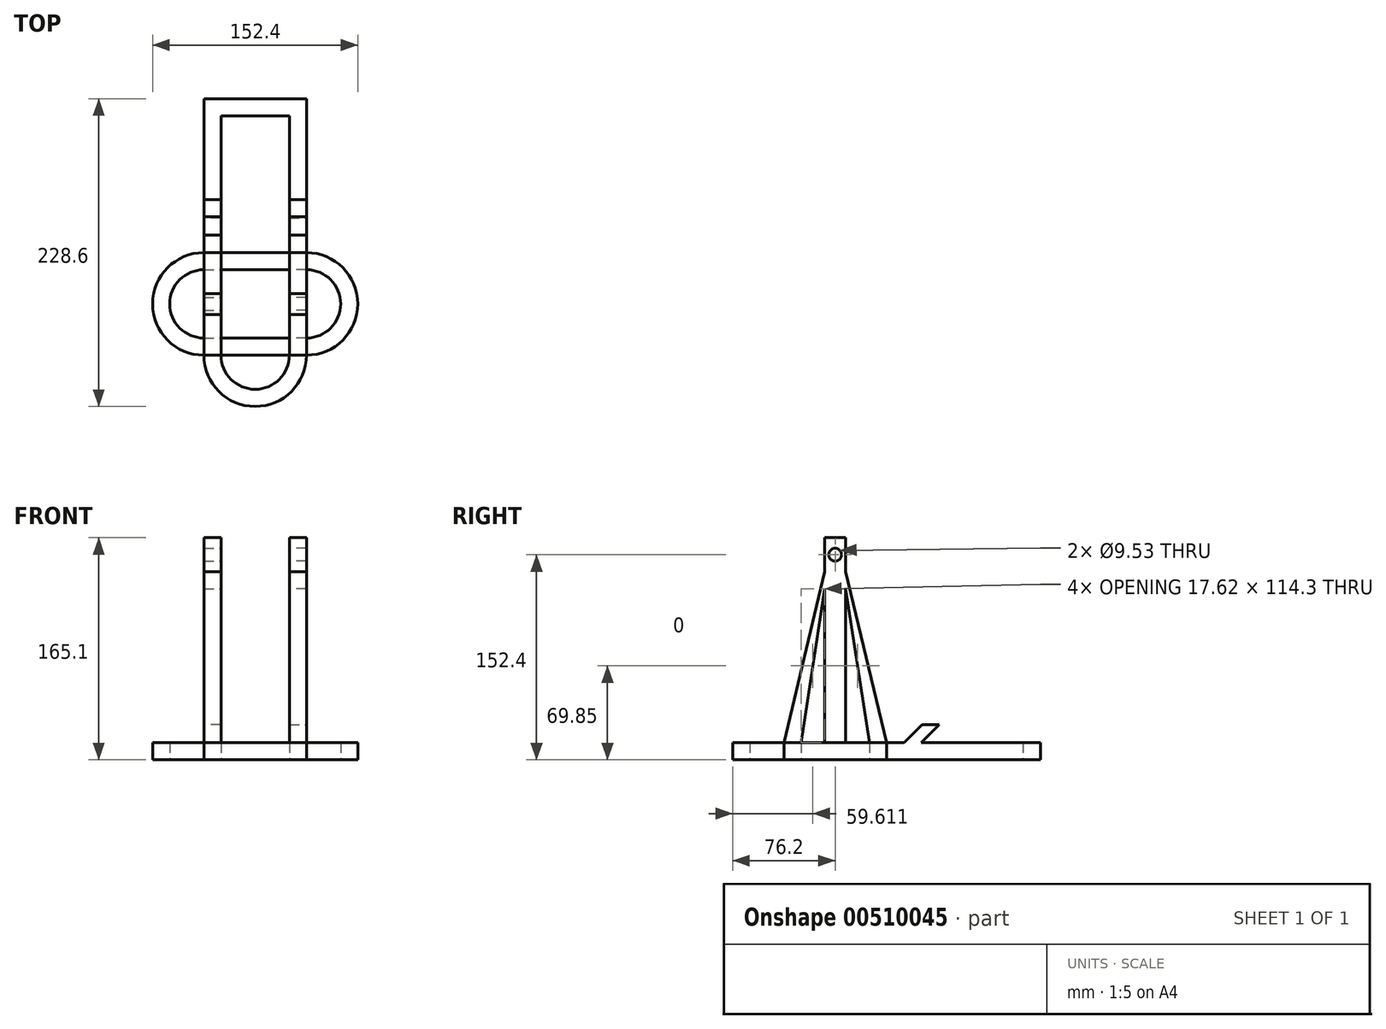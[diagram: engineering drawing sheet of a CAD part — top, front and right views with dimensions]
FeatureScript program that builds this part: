
annotation { "Feature Type Name" : "Feature", "Feature Type Description" : "" }
export const myFeature = defineFeature(function(context is Context, id is Id, definition is map)
    precondition{}
    {
        {
            var Q0;
            Q0=qCreatedBy(makeId("Top.planeOp"),FACE);
            var sketch = newSketch(context, id + "F0", { "sketchPlane" : qUnion([Q0])});
            skLineSegment(sketch, "E0.bottom", {"start": v(25.4, 38.1) * mm, "end": v(-25.4, 38.1) * mm});
            skLineSegment(sketch, "E0.top", {"start": v(38.1, -38.1) * mm, "end": v(-38.1, -38.1) * mm});
            skPoint(sketch, "E0.middle", {"position": v(0, 0) * mm});
            skArc(sketch, "E1", {"start": v(-38.1, 38.1) * mm, "mid": v(-76.2, 0) * mm, "end": v(-38.1, -38.1) * mm});
            skArc(sketch, "E2", {"start": v(38.1, -38.1) * mm, "mid": v(76.2, 0) * mm, "end": v(38.1, 38.1) * mm});
            skLineSegment(sketch, "E3.bottom", {"start": v(25.4, 25.4) * mm, "end": v(-25.4, 25.4) * mm});
            skLineSegment(sketch, "E3.top", {"start": v(25.4, -25.4) * mm, "end": v(-25.4, -25.4) * mm});
            skLineSegment(sketch, "E3.left", {"start": v(25.4, 25.4) * mm, "end": v(25.4, -25.4) * mm});
            skLineSegment(sketch, "E3.right", {"start": v(-25.4, 25.4) * mm, "end": v(-25.4, -25.4) * mm});
            skLineSegment(sketch, "E4", {"start": v(-38.1, 0) * mm, "end": v(-25.4, 0) * mm, "construction": true});
            skArc(sketch, "E5", {"start": v(-38.1, 25.4) * mm, "mid": v(-63.5, 0) * mm, "end": v(-38.1, -25.4) * mm});
            skArc(sketch, "E6", {"start": v(38.1, -25.4) * mm, "mid": v(63.5, 0) * mm, "end": v(38.1, 25.4) * mm});
            skLineSegment(sketch, "E7", {"start": v(-38.1, 25.4) * mm, "end": v(-38.1, -25.4) * mm});
            skLineSegment(sketch, "E8", {"start": v(38.1, 25.4) * mm, "end": v(38.1, -25.4) * mm});
            skLineSegment(sketch, "E9", {"start": v(25.4, 0) * mm, "end": v(38.1, 0) * mm});
            skLineSegment(sketch, "E10", {"start": v(0, 25.4) * mm, "end": v(0, 38.1) * mm, "construction": true});
            skLineSegment(sketch, "E11", {"start": v(-38.1, 38.1) * mm, "end": v(-38.1, 152.4) * mm});
            skLineSegment(sketch, "E12", {"start": v(25.4, 38.1) * mm, "end": v(25.4, 139.7) * mm});
            skLineSegment(sketch, "E13", {"start": v(38.1, 152.4) * mm, "end": v(38.1, 38.1) * mm});
            skLineSegment(sketch, "E14", {"start": v(-25.4, 139.7) * mm, "end": v(25.4, 139.7) * mm});
            skLineSegment(sketch, "E15.trimOffspring", {"start": v(-25.4, 139.7) * mm, "end": v(-25.4, 38.1) * mm});
            skLineSegment(sketch, "E16", {"start": v(0, 152.4) * mm, "end": v(0, 139.7) * mm});
            skLineSegment(sketch, "E17", {"start": v(-38.1, 152.4) * mm, "end": v(38.1, 152.4) * mm});
            skArc(sketch, "E18", {"start": v(-38.1, -38.1) * mm, "mid": v(0, -76.2) * mm, "end": v(38.1, -38.1) * mm});
            skArc(sketch, "E19", {"start": v(-25.4, -38.1) * mm, "mid": v(0, -63.5) * mm, "end": v(25.4, -38.1) * mm});
            skSolve(sketch);
        }
        {
            var Q0;
            Q0=makeQuery(id+"F0.imprint","IMPRINT",FACE,{"disambiguationData":[TD([[makeQuery(id+"F0.imprint","IMPRINT",EDGE,{"derivedFrom":sQuery(id+"F0.wireOp",EDGE,"E0.bottom")}),1.0]])]});
            var Q1;
            {var subQ0=sQuery(id+"F0.wireOp",EDGE,"E18");Q1=makeQuery(id+"F0.imprint","IMPRINT",FACE,{"disambiguationData":[TD([[makeQuery(id+"F0.imprint","IMPRINT",EDGE,{"derivedFrom":subQ0}),1.0]])]});}
            extrude(context, id + "F1", {"entities" : qUnion([Q0, Q1]), "depth" : 12.7 * mm});
        }
        {
            var Q0;
            Q0=makeQuery(id+"F1.opExtrude","CAP_FACE",FACE,{"disambiguationData":[OSD([sQuery(id+"F0.wireOp",EDGE,"E0.bottom"),sQuery(id+"F0.wireOp",EDGE,"E0.top"),sQuery(id+"F0.wireOp",EDGE,"E1"),sQuery(id+"F0.wireOp",EDGE,"E2"),sQuery(id+"F0.wireOp",EDGE,"E3.bottom"),sQuery(id+"F0.wireOp",EDGE,"E3.top"),sQuery(id+"F0.wireOp",EDGE,"E3.left"),sQuery(id+"F0.wireOp",EDGE,"E3.right"),sQuery(id+"F0.wireOp",EDGE,"E5"),sQuery(id+"F0.wireOp",EDGE,"E6"),sQuery(id+"F0.wireOp",EDGE,"E7"),sQuery(id+"F0.wireOp",EDGE,"E8"),sQuery(id+"F0.wireOp",EDGE,"E11"),sQuery(id+"F0.wireOp",EDGE,"eW0WrqK1-UAqt-hDgT-Up3a-L5sfFXZvn6og"),sQuery(id+"F0.wireOp",EDGE,"nnrCkwNE-DQRG-QEbR-UNsG-ga2bjcPdERez"),sQuery(id+"F0.wireOp",EDGE,"E12"),sQuery(id+"F0.wireOp",EDGE,"791204e0-3bb4-4a5e-b6f0-b63506c0d2d2"),sQuery(id+"F0.wireOp",EDGE,"E13"),sQuery(id+"F0.wireOp",EDGE,"E14"),sQuery(id+"F0.wireOp",EDGE,"Wew7rHin-LhuC-XoIG-YuWZ-GYeJMTqJVveu"),sQuery(id+"F0.wireOp",EDGE,"E15.trimOffspring"),sQuery(id+"F0.wireOp",EDGE,"b8e2c5c2-e6a5-42de-99a1-57f889a17564.trimOffspring")])],"isStart":false});
            var sketch = newSketch(context, id + "F2", { "sketchPlane" : qUnion([Q0])});
            skLineSegment(sketch, "E20.bottom", {"start": v(-25.4, 7.78) * mm, "end": v(-38.1, 7.78) * mm});
            skLineSegment(sketch, "E20.top", {"start": v(-25.4, -7.78) * mm, "end": v(-38.1, -7.78) * mm});
            skLineSegment(sketch, "E20.left", {"start": v(-25.4, 7.78) * mm, "end": v(-25.4, -7.78) * mm});
            skLineSegment(sketch, "E20.right", {"start": v(-38.1, 7.78) * mm, "end": v(-38.1, -7.78) * mm});
            skPoint(sketch, "E20.middle", {"position": v(-31.75, 0) * mm});
            skSolve(sketch);
        }
        {
            var Q0;
            Q0=qSketchRegion(id+"F2",true);
            extrude(context, id + "F3", {"entities" : qUnion([Q0]), "operationType" : NewBodyOperationType.ADD, "depth" : 152.4 * mm});
        }
        {
            var Q0;
            Q0=makeQuery(id+"F3.opExtrude","SWEPT_FACE",FACE,{"disambiguationData":[OSD([sQuery(id+"F2.wireOp",EDGE,"E20.top")])]});
            var sketch = newSketch(context, id + "F4", { "sketchPlane" : qUnion([Q0])});
            skLineSegment(sketch, "E21.bottom", {"start": v(-38.1, 139.7) * mm, "end": v(-25.4, 139.7) * mm});
            skLineSegment(sketch, "E21.top", {"start": v(-38.1, 127) * mm, "end": v(-25.4, 127) * mm});
            skLineSegment(sketch, "E21.left", {"start": v(-38.1, 139.7) * mm, "end": v(-38.1, 127) * mm});
            skLineSegment(sketch, "E21.right", {"start": v(-25.4, 139.7) * mm, "end": v(-25.4, 127) * mm});
            skSolve(sketch);
        }
        {
            var Q0;
            Q0=makeQuery(id+"F3.opExtrude","SWEPT_FACE",FACE,{"disambiguationData":[OSD([sQuery(id+"F2.wireOp",EDGE,"E20.bottom")])]});
            var sketch = newSketch(context, id + "F5", { "sketchPlane" : qUnion([Q0])});
            skLineSegment(sketch, "E22.0", {"start": v(25.4, 139.7) * mm, "end": v(25.4, 127) * mm});
            skLineSegment(sketch, "E23.0", {"start": v(38.1, 139.7) * mm, "end": v(25.4, 139.7) * mm});
            skLineSegment(sketch, "E24.0", {"start": v(38.1, 127) * mm, "end": v(25.4, 127) * mm});
            skLineSegment(sketch, "E25.0", {"start": v(38.1, 139.7) * mm, "end": v(38.1, 127) * mm});
            skSolve(sketch);
        }
        {
            var Q0;
            Q0=makeQuery(id+"F1.opExtrude","CAP_FACE",FACE,{"disambiguationData":[OSD([sQuery(id+"F0.wireOp",EDGE,"E0.bottom"),sQuery(id+"F0.wireOp",EDGE,"E0.top"),sQuery(id+"F0.wireOp",EDGE,"E1"),sQuery(id+"F0.wireOp",EDGE,"E2"),sQuery(id+"F0.wireOp",EDGE,"E3.bottom"),sQuery(id+"F0.wireOp",EDGE,"E3.top"),sQuery(id+"F0.wireOp",EDGE,"E3.left"),sQuery(id+"F0.wireOp",EDGE,"E3.right"),sQuery(id+"F0.wireOp",EDGE,"E5"),sQuery(id+"F0.wireOp",EDGE,"E6"),sQuery(id+"F0.wireOp",EDGE,"E7"),sQuery(id+"F0.wireOp",EDGE,"E8"),sQuery(id+"F0.wireOp",EDGE,"E11"),sQuery(id+"F0.wireOp",EDGE,"eW0WrqK1-UAqt-hDgT-Up3a-L5sfFXZvn6og"),sQuery(id+"F0.wireOp",EDGE,"nnrCkwNE-DQRG-QEbR-UNsG-ga2bjcPdERez"),sQuery(id+"F0.wireOp",EDGE,"E12"),sQuery(id+"F0.wireOp",EDGE,"791204e0-3bb4-4a5e-b6f0-b63506c0d2d2"),sQuery(id+"F0.wireOp",EDGE,"E13"),sQuery(id+"F0.wireOp",EDGE,"E14"),sQuery(id+"F0.wireOp",EDGE,"Wew7rHin-LhuC-XoIG-YuWZ-GYeJMTqJVveu"),sQuery(id+"F0.wireOp",EDGE,"E15.trimOffspring"),sQuery(id+"F0.wireOp",EDGE,"b8e2c5c2-e6a5-42de-99a1-57f889a17564.trimOffspring")])],"isStart":false});
            var sketch = newSketch(context, id + "F6", { "sketchPlane" : qUnion([Q0])});
            skPoint(sketch, "E26.oppositeSnap0", {"position": v(-25.4, -16.59) * mm});
            skLineSegment(sketch, "E26.bottom", {"start": v(-38.1, -25.4) * mm, "end": v(-25.4, -25.4) * mm});
            skLineSegment(sketch, "E26.top", {"start": v(-38.1, -38.1) * mm, "end": v(-25.4, -38.1) * mm});
            skLineSegment(sketch, "E26.left", {"start": v(-38.1, -25.4) * mm, "end": v(-38.1, -38.1) * mm});
            skLineSegment(sketch, "E26.right", {"start": v(-25.4, -25.4) * mm, "end": v(-25.4, -38.1) * mm});
            skLineSegment(sketch, "E27.bottom", {"start": v(-38.1, 38.1) * mm, "end": v(-25.4, 38.1) * mm});
            skLineSegment(sketch, "E27.top", {"start": v(-38.1, 25.4) * mm, "end": v(-25.4, 25.4) * mm});
            skLineSegment(sketch, "E27.left", {"start": v(-38.1, 38.1) * mm, "end": v(-38.1, 25.4) * mm});
            skLineSegment(sketch, "E27.right", {"start": v(-25.4, 38.1) * mm, "end": v(-25.4, 25.4) * mm});
            skArc(sketch, "E28.0", {"start": v(-38.1, 25.4) * mm, "mid": v(-63.5, 0) * mm, "end": v(-38.1, -25.4) * mm});
            skArc(sketch, "E29.0", {"start": v(-38.1, 38.1) * mm, "mid": v(-76.2, 0) * mm, "end": v(-38.1, -38.1) * mm});
            skSolve(sketch);
        }
        {
            var Q1;
            Q1=makeQuery(id+"F5.imprint","IMPRINT",FACE,{"disambiguationData":[TD([[makeQuery(id+"F5.imprint","IMPRINT",EDGE,{"derivedFrom":sQuery(id+"F5.wireOp",EDGE,"E22.0")}),1.0]])]});
            var Q2;
            Q2=makeQuery(id+"F6.imprint","IMPRINT",FACE,{"disambiguationData":[TD([[makeQuery(id+"F6.imprint","IMPRINT",EDGE,{"derivedFrom":sQuery(id+"F6.wireOp",EDGE,"E27.bottom")}),-1.0]])]});
            loft(context, id + "F7", {"operationType" : NewBodyOperationType.ADD, "sheetProfilesArray" : [{ "sheetProfileEntities" : qUnion([Q1]) }, { "sheetProfileEntities" : qUnion([Q2]) }]});
        }
        {
            var Q1;
            Q1=makeQuery(id+"F6.imprint","IMPRINT",FACE,{"disambiguationData":[TD([[makeQuery(id+"F6.imprint","IMPRINT",EDGE,{"derivedFrom":sQuery(id+"F6.wireOp",EDGE,"E26.bottom")}),-1.0]])]});
            var Q2;
            Q2=makeQuery(id+"F4.imprint","IMPRINT",FACE,{"disambiguationData":[TD([[makeQuery(id+"F4.imprint","IMPRINT",EDGE,{"derivedFrom":sQuery(id+"F4.wireOp",EDGE,"E21.bottom")}),-1.0]])]});
            loft(context, id + "F8", {"operationType" : NewBodyOperationType.ADD, "sheetProfilesArray" : [{ "sheetProfileEntities" : qUnion([Q1]) }, { "sheetProfileEntities" : qUnion([Q2]) }]});
        }
        {
            var Q0;
            Q0=makeQuery(id+"F1.opExtrude","SWEPT_FACE",FACE,{"disambiguationData":[OSD([sQuery(id+"F0.wireOp",EDGE,"E11")])]});
            var sketch = newSketch(context, id + "F9", { "sketchPlane" : qUnion([Q0])});
            skLineSegment(sketch, "E30", {"start": v(-63.94, 12.7) * mm, "end": v(-77.41, 26.17) * mm});
            skLineSegment(sketch, "E31", {"start": v(-77.41, 26.17) * mm, "end": v(-64.71, 26.17) * mm});
            skLineSegment(sketch, "E32", {"start": v(-64.71, 26.17) * mm, "end": v(-51.24, 12.7) * mm});
            skSolve(sketch);
        }
        {
            var Q0;
            {var subQ0=sQuery(id+"F9.wireOp",EDGE,"E30");Q0=makeQuery(id+"F9.imprint","IMPRINT",FACE,{"disambiguationData":[TD([[makeQuery(id+"F9.imprint","IMPRINT",EDGE,{"derivedFrom":subQ0}),-1.0]])]});}
            var Q1;
            Q1=makeQuery(id+"F1.opExtrude","SWEPT_FACE",FACE,{"disambiguationData":[OSD([sQuery(id+"F0.wireOp",EDGE,"E15.trimOffspring")])]});
            extrude(context, id + "F10", {"entities" : qUnion([Q0]), "operationType" : NewBodyOperationType.ADD, "endBound" : BoundingType.UP_TO_SURFACE, "oppositeDirection" : true, "endBoundEntityFace" : qUnion([Q1]), "depth" : 25.4 * mm});
        }
        {
            var Q0;
            {var subQ0=sQuery(id+"F2.wireOp",EDGE,"E20.left");var subQ1=sQuery(id+"F0.wireOp",EDGE,"E3.right");Q0=makeQuery(id+"F8.boolean.opBoolean","MERGE",FACE,{"derivedFrom":[makeQuery(id+"F7.boolean.opBoolean","MERGE",FACE,{"derivedFrom":[makeQuery(id+"F3.boolean.opBoolean","MERGE",FACE,{"derivedFrom":[makeQuery(id+"F1.opExtrude","SWEPT_FACE",FACE,{"disambiguationData":[OSD([subQ1])]}),makeQuery(id+"F3.opExtrude","SWEPT_FACE",FACE,{"disambiguationData":[OSD([subQ0])]})]}),makeQuery(id+"F7.opLoft","SWEPT_FACE",FACE,{"disambiguationData":[OSD([sQuery(id+"F0.wireOp",EDGE,"E0.bottom"),sQuery(id+"F0.wireOp",EDGE,"E3.bottom"),subQ1,sQuery(id+"F0.wireOp",EDGE,"E15.trimOffspring"),sQuery(id+"F2.wireOp",EDGE,"E20.bottom"),subQ0,sQuery(id+"F5.wireOp",EDGE,"E22.0"),sQuery(id+"F5.wireOp",EDGE,"E23.0"),sQuery(id+"F5.wireOp",EDGE,"E24.0"),sQuery(id+"F6.wireOp",EDGE,"E27.bottom"),sQuery(id+"F6.wireOp",EDGE,"E27.top"),sQuery(id+"F6.wireOp",EDGE,"E27.right")])]})]}),makeQuery(id+"F8.opLoft","SWEPT_FACE",FACE,{"disambiguationData":[OSD([sQuery(id+"F0.wireOp",EDGE,"E0.top"),sQuery(id+"F0.wireOp",EDGE,"E3.top"),subQ1,sQuery(id+"F0.wireOp",EDGE,"E19"),sQuery(id+"F2.wireOp",EDGE,"E20.top"),subQ0,sQuery(id+"F4.wireOp",EDGE,"E21.bottom"),sQuery(id+"F4.wireOp",EDGE,"E21.top"),sQuery(id+"F4.wireOp",EDGE,"E21.right"),sQuery(id+"F6.wireOp",EDGE,"E26.bottom"),sQuery(id+"F6.wireOp",EDGE,"E26.top"),sQuery(id+"F6.wireOp",EDGE,"E26.right")])]})]});}
            var sketch = newSketch(context, id + "F11", { "sketchPlane" : qUnion([Q0])});
            skLineSegment(sketch, "E33", {"start": v(0, 165.1) * mm, "end": v(0, 139.7) * mm, "construction": true});
            skCircle(sketch, "E34", {"center": v(0, 152.4) * mm, "radius": 4.76 * mm});
            skSolve(sketch);
        }
        {
            var Q0;
            Q0=makeQuery(id+"F11.imprint","IMPRINT",FACE,{"disambiguationData":[TD([[makeQuery(id+"F11.imprint","IMPRINT",EDGE,{"derivedFrom":sQuery(id+"F11.wireOp",EDGE,"E34")}),1.0]])]});
            var Q1;
            Q1=sQuery(id+"F11.wireOp",EDGE,"E34");
            extrude(context, id + "F12", {"entities" : qUnion([Q0]), "operationType" : NewBodyOperationType.REMOVE, "surfaceEntities" : qUnion([Q1]), "endBound" : BoundingType.THROUGH_ALL, "oppositeDirection" : true, "depth" : 25.4 * mm});
        }
        {
            var Q0;
            Q0=makeQuery(id+"F1.opExtrude","SWEPT_BODY",BODY,{"disambiguationData":[OSD([sQuery(id+"F0.wireOp",EDGE,"E0.bottom"),sQuery(id+"F0.wireOp",EDGE,"E0.top"),sQuery(id+"F0.wireOp",EDGE,"E1"),sQuery(id+"F0.wireOp",EDGE,"E2"),sQuery(id+"F0.wireOp",EDGE,"E3.bottom"),sQuery(id+"F0.wireOp",EDGE,"E3.top"),sQuery(id+"F0.wireOp",EDGE,"E3.left"),sQuery(id+"F0.wireOp",EDGE,"E3.right"),sQuery(id+"F0.wireOp",EDGE,"E5"),sQuery(id+"F0.wireOp",EDGE,"E6"),sQuery(id+"F0.wireOp",EDGE,"E7"),sQuery(id+"F0.wireOp",EDGE,"E8"),sQuery(id+"F0.wireOp",EDGE,"E11"),sQuery(id+"F0.wireOp",EDGE,"E12"),sQuery(id+"F0.wireOp",EDGE,"791204e0-3bb4-4a5e-b6f0-b63506c0d2d2"),sQuery(id+"F0.wireOp",EDGE,"E13"),sQuery(id+"F0.wireOp",EDGE,"E14"),sQuery(id+"F0.wireOp",EDGE,"Wew7rHin-LhuC-XoIG-YuWZ-GYeJMTqJVveu"),sQuery(id+"F0.wireOp",EDGE,"E15.trimOffspring"),sQuery(id+"F0.wireOp",EDGE,"b8e2c5c2-e6a5-42de-99a1-57f889a17564.trimOffspring"),sQuery(id+"F0.wireOp",EDGE,"2s5irlIo-1hsk-PBSL-bw71-EGN7Nmvhz8i4"),sQuery(id+"F0.wireOp",EDGE,"WOsVuXmC-js16-euqo-qlyW-9Vxgc6dwlDmT")])]});
            var Q1;
            Q1=qCreatedBy(makeId("Right.planeOp"),FACE);
            mirror(context, id + "F13", {"operationType" : NewBodyOperationType.ADD, "entities" : qUnion([Q0]), "mirrorPlane" : qUnion([Q1])});
        }
    });
